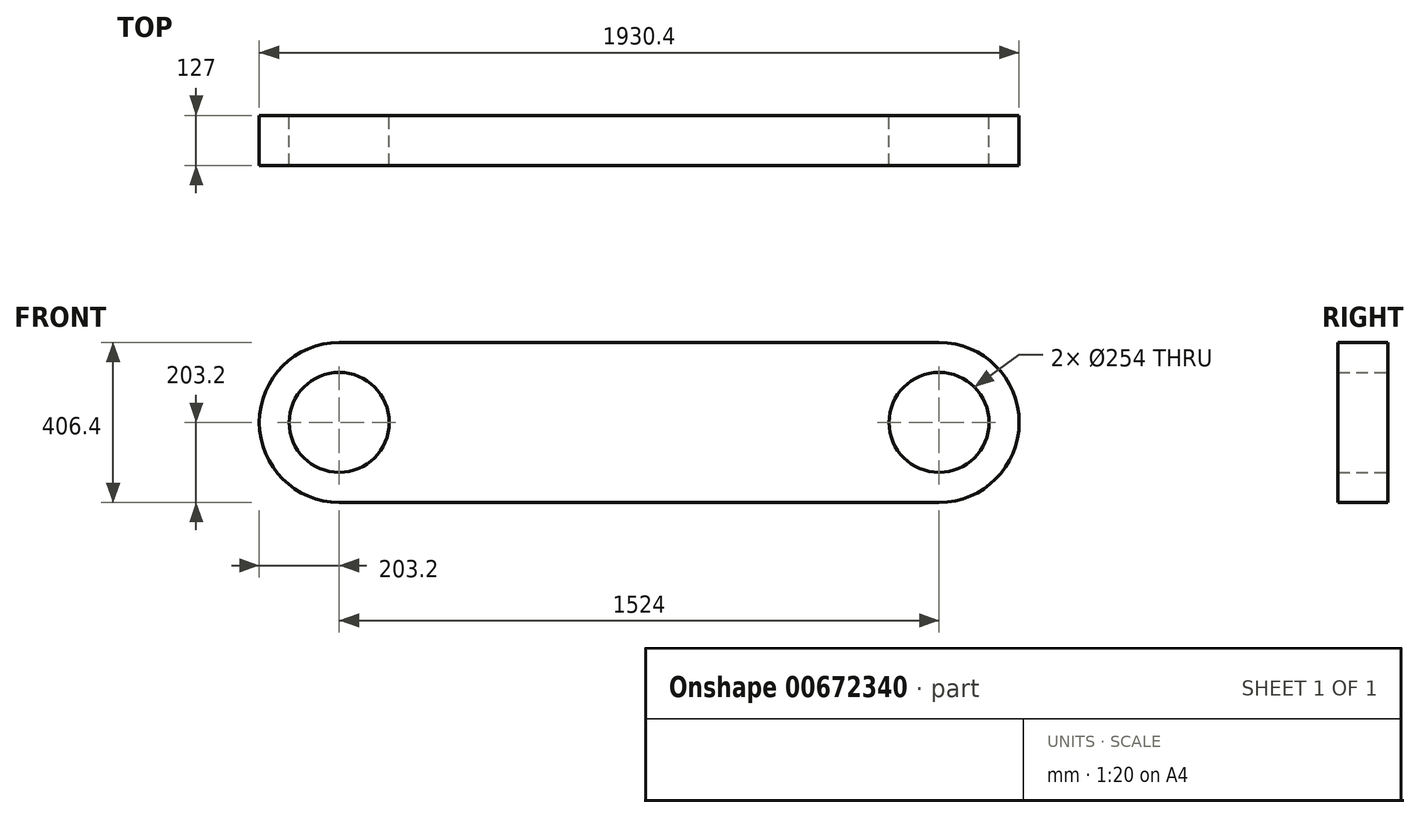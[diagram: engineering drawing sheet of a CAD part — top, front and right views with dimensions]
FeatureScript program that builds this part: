
annotation { "Feature Type Name" : "Feature", "Feature Type Description" : "" }
export const myFeature = defineFeature(function(context is Context, id is Id, definition is map)
    precondition{}
    {
        {
            var Q0;
            Q0=qCreatedBy(makeId("Front.planeOp"),FACE);
            var sketch = newSketch(context, id + "F0", { "sketchPlane" : qUnion([Q0])});
            skLineSegment(sketch, "E0.bottom", {"start": v(-762, 203.2) * mm, "end": v(762, 203.2) * mm});
            skLineSegment(sketch, "E0.top", {"start": v(-762, -203.2) * mm, "end": v(762, -203.2) * mm});
            skArc(sketch, "E1", {"start": v(-762, 203.2) * mm, "mid": v(-965.2, 0) * mm, "end": v(-762, -203.2) * mm});
            skArc(sketch, "E2", {"start": v(762, -203.2) * mm, "mid": v(965.2, 0) * mm, "end": v(762, 203.2) * mm});
            skCircle(sketch, "E3", {"center": v(-762, 0) * mm, "radius": 127 * mm});
            skCircle(sketch, "E4", {"center": v(762, 0) * mm, "radius": 127 * mm});
            skSolve(sketch);
        }
        {
            var Q0;
            Q0 = qSketchRegion(id + "F0", true);
            extrude(context, id + "F1", {"entities" : qUnion([Q0]), "depth" : 127 * mm, "offsetDistance" : 25.4 * mm});
        }
    });
